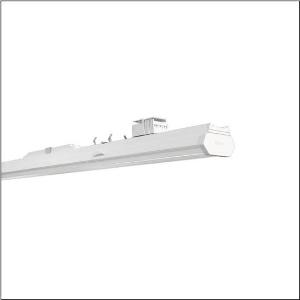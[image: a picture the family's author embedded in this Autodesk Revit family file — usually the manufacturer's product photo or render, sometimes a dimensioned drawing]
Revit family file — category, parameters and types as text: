
# Revit family: licross_r__11_protected_ho_51tp13dn4f5s_0b0f
name_source: partatom
category: Lighting Fixtures
units: mm (PartAtom-declared; Revit-internal decimal feet)

## family parameters
Cut with Voids When Loaded = No
Host = Face
Light Source = No
Part Type = Normal
Room Calculation Point = No
Round Connector Dimension = Use Diameter
Shared = No

## types (1)
- --- (1 x LED, 15550 lm, 87.3 W, 4000K)
    Apparent Load = 87 VA
    CIE Flux Codes = 89 96 99 100 99
    Color Rendering = 80
    Color Temperature = 4000K
    Default Elevation = 1800 mm
    Description = Licross® 11 Protected HO, luminaire insert, of sheet steel, galvanised, coil coated, white, length: 1.500mm, width: 90mm, height: 101mm, LED rated luminous flux: 15.550lm, light colour: 840, control gear: DALI 2, with plug, 5-pole, with phase selection, mains connection: 220..240V, AC, 50/60Hz, rated input power: 87W, halogen-free wiring, primary light control with lens, of plastic, primary optical cover: cover, of PMMA, light emission: direct distribution, primary light characteristic: symmetric, protection rating (complete): IP64, insulation class (complete): insulation class I (protective earthing), certification: CE, ENEC, VDE, UKCA, protection symbol: D if used in an environment with conductive dust loads with corresponding accessories, impact resistance: IK06, permissible ambient temperature for indoor applications: -25..+30°C, corresponds to IFS (International Featured Standards) requirements for safety and quality in the food industry, reducing of maximum allowable ambient temperature of 5°C with ceiling mounting, LABS conformity tested according to VDMA 24364:2018-05, packaging unit: 1 piece
    Height = 92 mm
    Lamp = 1 x LED
    Lamp Light Flux = 15550 lm
    Lamp Power = 87.3 W
    Lamp count = 1
    Length = 1500 mm
    Luminous efficacy = 178 lm/W
    Manufacturer = Siteco
    ModVariant = No
    Model = 51TP13DN4F5S
    Mounting Place = Ceiling
    Mounting Type = Pendant
    Number of Poles = 1
    OnlyDefault = Yes
    Power Factor = 1
    Product Name = Licross® 11 Protected HO
    Product group = luminaire insert
    ProductGroupID = 901
    Protection Class = Protection class I
    Protection Degree = IP 64
    RLX_Detail_Level = 1
    RLX_Emergency_Light_Flux = 0 lm
    RLX_Emergency_Type = 0
    RLX_Emergency_Type_DB = No
    RlxData = <blob elided: 24205 chars, md5=5831f383>
    Socket = socket
    Standby Power = 0 W
    System Light Flux = 15550 lm
    System Power = 87 W
    Type Comments = factory setting: luminous flux: 100 % | dim-lin: 254 | 589 mA
    Type Image = l_1256148.jpg
    URL = http://relux.com
    VarID = @adj_049131
    Voltage = 0 V
    Weight = 0.00 kg
    Width = 88 mm

## geometry (parser evidence)
native form markers: Blend x4, Sweep x12
no freeform markers — native parametric forms only
